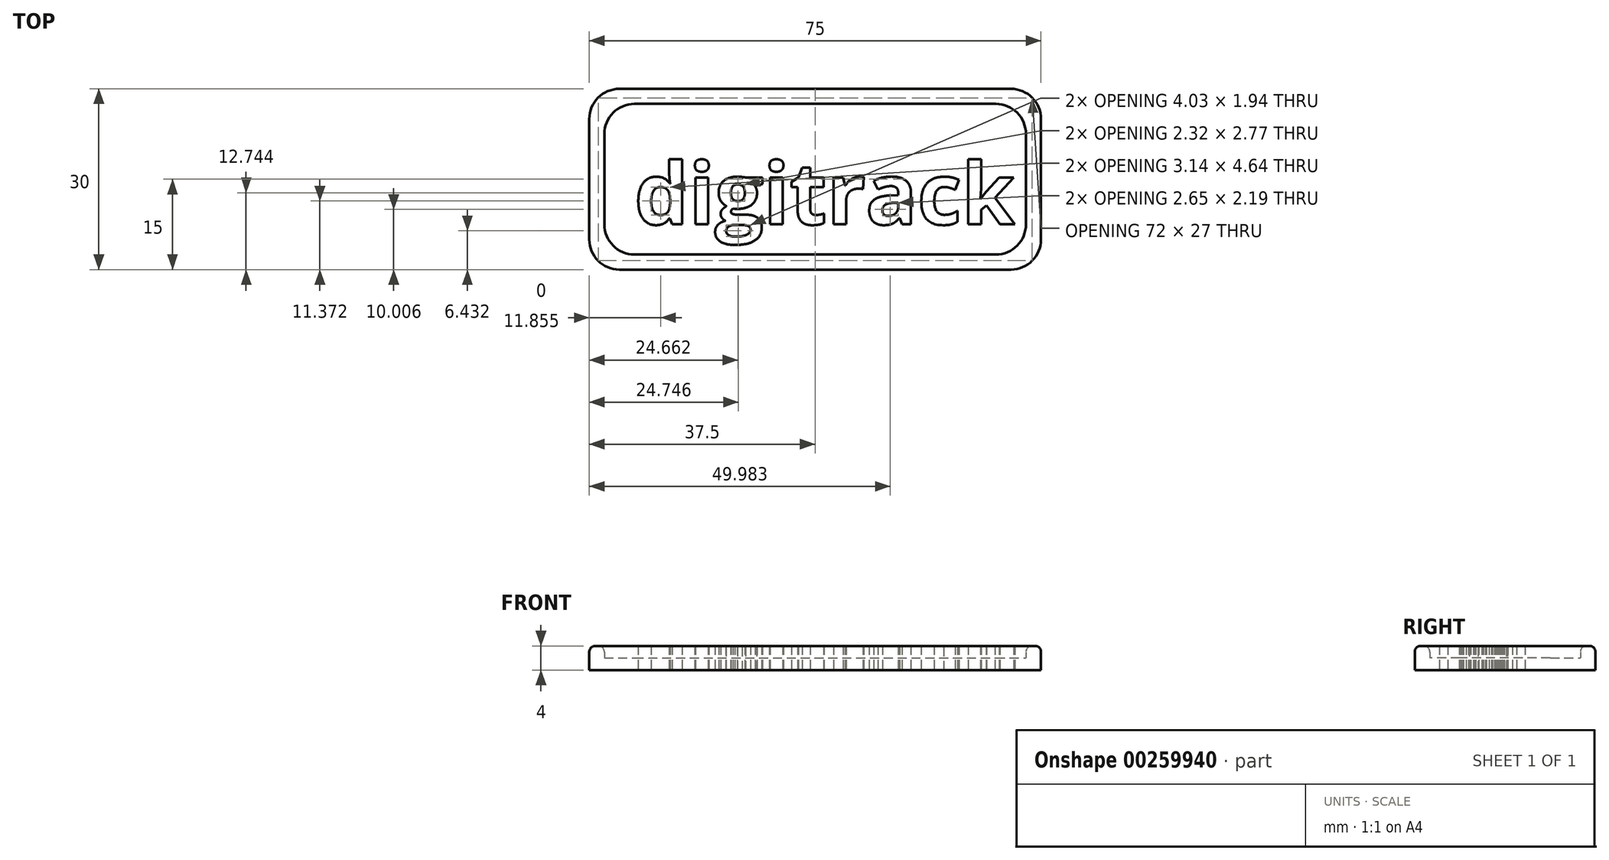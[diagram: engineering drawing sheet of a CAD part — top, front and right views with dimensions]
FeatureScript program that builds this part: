
annotation { "Feature Type Name" : "Feature", "Feature Type Description" : "" }
export const myFeature = defineFeature(function(context is Context, id is Id, definition is map)
    precondition{}
    {
        {
            var Q0;
            Q0=qCreatedBy(makeId("Top.planeOp"),FACE);
            var sketch = newSketch(context, id + "F0", { "sketchPlane" : qUnion([Q0])});
            skText(sketch, "E0", { "text": "digitrack", "fontName": "OpenSans-Bold.ttf"});
            const initialGuessF0  = {"E0": [0, 0, 1, 0, 0.0205]};
            skSetInitialGuess(sketch, initialGuessF0);
            skSolve(sketch);
        }
        {
            var Q0;
            Q0 = qSketchRegion(id + "F0", true);
            extrude(context, id + "F1", {"entities" : qUnion([Q0]), "depth" : 8 * mm});
        }
        {
            var Q0;
            Q0=makeQuery(id+"F1.opExtrude","SWEPT_BODY",BODY,{"disambiguationData":[OSD([sQuery(id+"F0.wireOp",EDGE,"E0.sketch_text.stroke-0"),sQuery(id+"F0.wireOp",EDGE,"E0.sketch_text.stroke-1"),sQuery(id+"F0.wireOp",EDGE,"E0.sketch_text.stroke-2"),sQuery(id+"F0.wireOp",EDGE,"E0.sketch_text.stroke-3"),sQuery(id+"F0.wireOp",EDGE,"E0.sketch_text.stroke-4"),sQuery(id+"F0.wireOp",EDGE,"E0.sketch_text.stroke-5"),sQuery(id+"F0.wireOp",EDGE,"E0.sketch_text.stroke-6"),sQuery(id+"F0.wireOp",EDGE,"E0.sketch_text.stroke-7"),sQuery(id+"F0.wireOp",EDGE,"E0.sketch_text.stroke-8"),sQuery(id+"F0.wireOp",EDGE,"E0.sketch_text.stroke-9"),sQuery(id+"F0.wireOp",EDGE,"E0.sketch_text.stroke-10"),sQuery(id+"F0.wireOp",EDGE,"E0.sketch_text.stroke-11"),sQuery(id+"F0.wireOp",EDGE,"E0.sketch_text.stroke-12"),sQuery(id+"F0.wireOp",EDGE,"E0.sketch_text.stroke-13"),sQuery(id+"F0.wireOp",EDGE,"E0.sketch_text.stroke-14"),sQuery(id+"F0.wireOp",EDGE,"E0.sketch_text.stroke-15"),sQuery(id+"F0.wireOp",EDGE,"E0.sketch_text.stroke-16"),sQuery(id+"F0.wireOp",EDGE,"E0.sketch_text.stroke-17"),sQuery(id+"F0.wireOp",EDGE,"E0.sketch_text.stroke-18"),sQuery(id+"F0.wireOp",EDGE,"E0.sketch_text.stroke-19"),sQuery(id+"F0.wireOp",EDGE,"E0.sketch_text.stroke-20"),sQuery(id+"F0.wireOp",EDGE,"E0.sketch_text.stroke-21"),sQuery(id+"F0.wireOp",EDGE,"E0.sketch_text.stroke-22")])]});
            var Q1;
            Q1=makeQuery(id+"F1.opExtrude","SWEPT_BODY",BODY,{"disambiguationData":[OSD([sQuery(id+"F0.wireOp",EDGE,"E0.sketch_text.stroke-23"),sQuery(id+"F0.wireOp",EDGE,"E0.sketch_text.stroke-24"),sQuery(id+"F0.wireOp",EDGE,"E0.sketch_text.stroke-25"),sQuery(id+"F0.wireOp",EDGE,"E0.sketch_text.stroke-26"),sQuery(id+"F0.wireOp",EDGE,"E0.sketch_text.stroke-27")])]});
            var Q2;
            Q2=makeQuery(id+"F1.opExtrude","SWEPT_BODY",BODY,{"disambiguationData":[OSD([sQuery(id+"F0.wireOp",EDGE,"E0.sketch_text.stroke-28"),sQuery(id+"F0.wireOp",EDGE,"E0.sketch_text.stroke-29"),sQuery(id+"F0.wireOp",EDGE,"E0.sketch_text.stroke-30"),sQuery(id+"F0.wireOp",EDGE,"E0.sketch_text.stroke-31")])]});
            var Q3;
            Q3=makeQuery(id+"F1.opExtrude","SWEPT_BODY",BODY,{"disambiguationData":[OSD([sQuery(id+"F0.wireOp",EDGE,"E0.sketch_text.stroke-32"),sQuery(id+"F0.wireOp",EDGE,"E0.sketch_text.stroke-33"),sQuery(id+"F0.wireOp",EDGE,"E0.sketch_text.stroke-34"),sQuery(id+"F0.wireOp",EDGE,"E0.sketch_text.stroke-35"),sQuery(id+"F0.wireOp",EDGE,"E0.sketch_text.stroke-36"),sQuery(id+"F0.wireOp",EDGE,"E0.sketch_text.stroke-37"),sQuery(id+"F0.wireOp",EDGE,"E0.sketch_text.stroke-38"),sQuery(id+"F0.wireOp",EDGE,"E0.sketch_text.stroke-39"),sQuery(id+"F0.wireOp",EDGE,"E0.sketch_text.stroke-40"),sQuery(id+"F0.wireOp",EDGE,"E0.sketch_text.stroke-41"),sQuery(id+"F0.wireOp",EDGE,"E0.sketch_text.stroke-42"),sQuery(id+"F0.wireOp",EDGE,"E0.sketch_text.stroke-43"),sQuery(id+"F0.wireOp",EDGE,"E0.sketch_text.stroke-44"),sQuery(id+"F0.wireOp",EDGE,"E0.sketch_text.stroke-45"),sQuery(id+"F0.wireOp",EDGE,"E0.sketch_text.stroke-46"),sQuery(id+"F0.wireOp",EDGE,"E0.sketch_text.stroke-47"),sQuery(id+"F0.wireOp",EDGE,"E0.sketch_text.stroke-48"),sQuery(id+"F0.wireOp",EDGE,"E0.sketch_text.stroke-49"),sQuery(id+"F0.wireOp",EDGE,"E0.sketch_text.stroke-50"),sQuery(id+"F0.wireOp",EDGE,"E0.sketch_text.stroke-51"),sQuery(id+"F0.wireOp",EDGE,"E0.sketch_text.stroke-52"),sQuery(id+"F0.wireOp",EDGE,"E0.sketch_text.stroke-53"),sQuery(id+"F0.wireOp",EDGE,"E0.sketch_text.stroke-54"),sQuery(id+"F0.wireOp",EDGE,"E0.sketch_text.stroke-55"),sQuery(id+"F0.wireOp",EDGE,"E0.sketch_text.stroke-56"),sQuery(id+"F0.wireOp",EDGE,"E0.sketch_text.stroke-57"),sQuery(id+"F0.wireOp",EDGE,"E0.sketch_text.stroke-58"),sQuery(id+"F0.wireOp",EDGE,"E0.sketch_text.stroke-59"),sQuery(id+"F0.wireOp",EDGE,"E0.sketch_text.stroke-60"),sQuery(id+"F0.wireOp",EDGE,"E0.sketch_text.stroke-61"),sQuery(id+"F0.wireOp",EDGE,"E0.sketch_text.stroke-62"),sQuery(id+"F0.wireOp",EDGE,"E0.sketch_text.stroke-63"),sQuery(id+"F0.wireOp",EDGE,"E0.sketch_text.stroke-64"),sQuery(id+"F0.wireOp",EDGE,"E0.sketch_text.stroke-65"),sQuery(id+"F0.wireOp",EDGE,"E0.sketch_text.stroke-66"),sQuery(id+"F0.wireOp",EDGE,"E0.sketch_text.stroke-67"),sQuery(id+"F0.wireOp",EDGE,"E0.sketch_text.stroke-68"),sQuery(id+"F0.wireOp",EDGE,"E0.sketch_text.stroke-69"),sQuery(id+"F0.wireOp",EDGE,"E0.sketch_text.stroke-70"),sQuery(id+"F0.wireOp",EDGE,"E0.sketch_text.stroke-71"),sQuery(id+"F0.wireOp",EDGE,"E0.sketch_text.stroke-72"),sQuery(id+"F0.wireOp",EDGE,"E0.sketch_text.stroke-73"),sQuery(id+"F0.wireOp",EDGE,"E0.sketch_text.stroke-74"),sQuery(id+"F0.wireOp",EDGE,"E0.sketch_text.stroke-75")])]});
            var Q4;
            Q4=makeQuery(id+"F1.opExtrude","SWEPT_BODY",BODY,{"disambiguationData":[OSD([sQuery(id+"F0.wireOp",EDGE,"E0.sketch_text.stroke-76"),sQuery(id+"F0.wireOp",EDGE,"E0.sketch_text.stroke-77"),sQuery(id+"F0.wireOp",EDGE,"E0.sketch_text.stroke-78"),sQuery(id+"F0.wireOp",EDGE,"E0.sketch_text.stroke-79"),sQuery(id+"F0.wireOp",EDGE,"E0.sketch_text.stroke-80")])]});
            var Q5;
            Q5=makeQuery(id+"F1.opExtrude","SWEPT_BODY",BODY,{"disambiguationData":[OSD([sQuery(id+"F0.wireOp",EDGE,"E0.sketch_text.stroke-81"),sQuery(id+"F0.wireOp",EDGE,"E0.sketch_text.stroke-82"),sQuery(id+"F0.wireOp",EDGE,"E0.sketch_text.stroke-83"),sQuery(id+"F0.wireOp",EDGE,"E0.sketch_text.stroke-84")])]});
            var Q6;
            Q6=makeQuery(id+"F1.opExtrude","SWEPT_BODY",BODY,{"disambiguationData":[OSD([sQuery(id+"F0.wireOp",EDGE,"E0.sketch_text.stroke-85"),sQuery(id+"F0.wireOp",EDGE,"E0.sketch_text.stroke-86"),sQuery(id+"F0.wireOp",EDGE,"E0.sketch_text.stroke-87"),sQuery(id+"F0.wireOp",EDGE,"E0.sketch_text.stroke-88"),sQuery(id+"F0.wireOp",EDGE,"E0.sketch_text.stroke-89"),sQuery(id+"F0.wireOp",EDGE,"E0.sketch_text.stroke-90"),sQuery(id+"F0.wireOp",EDGE,"E0.sketch_text.stroke-91"),sQuery(id+"F0.wireOp",EDGE,"E0.sketch_text.stroke-92"),sQuery(id+"F0.wireOp",EDGE,"E0.sketch_text.stroke-93"),sQuery(id+"F0.wireOp",EDGE,"E0.sketch_text.stroke-94"),sQuery(id+"F0.wireOp",EDGE,"E0.sketch_text.stroke-95"),sQuery(id+"F0.wireOp",EDGE,"E0.sketch_text.stroke-96"),sQuery(id+"F0.wireOp",EDGE,"E0.sketch_text.stroke-97"),sQuery(id+"F0.wireOp",EDGE,"E0.sketch_text.stroke-98"),sQuery(id+"F0.wireOp",EDGE,"E0.sketch_text.stroke-99"),sQuery(id+"F0.wireOp",EDGE,"E0.sketch_text.stroke-100"),sQuery(id+"F0.wireOp",EDGE,"E0.sketch_text.stroke-101"),sQuery(id+"F0.wireOp",EDGE,"E0.sketch_text.stroke-102")])]});
            var Q7;
            Q7=makeQuery(id+"F1.opExtrude","SWEPT_BODY",BODY,{"disambiguationData":[OSD([sQuery(id+"F0.wireOp",EDGE,"E0.sketch_text.stroke-103"),sQuery(id+"F0.wireOp",EDGE,"E0.sketch_text.stroke-104"),sQuery(id+"F0.wireOp",EDGE,"E0.sketch_text.stroke-105"),sQuery(id+"F0.wireOp",EDGE,"E0.sketch_text.stroke-106"),sQuery(id+"F0.wireOp",EDGE,"E0.sketch_text.stroke-107"),sQuery(id+"F0.wireOp",EDGE,"E0.sketch_text.stroke-108"),sQuery(id+"F0.wireOp",EDGE,"E0.sketch_text.stroke-109"),sQuery(id+"F0.wireOp",EDGE,"E0.sketch_text.stroke-110"),sQuery(id+"F0.wireOp",EDGE,"E0.sketch_text.stroke-111"),sQuery(id+"F0.wireOp",EDGE,"E0.sketch_text.stroke-112"),sQuery(id+"F0.wireOp",EDGE,"E0.sketch_text.stroke-113"),sQuery(id+"F0.wireOp",EDGE,"E0.sketch_text.stroke-114"),sQuery(id+"F0.wireOp",EDGE,"E0.sketch_text.stroke-115")])]});
            var Q8;
            Q8=makeQuery(id+"F1.opExtrude","SWEPT_BODY",BODY,{"disambiguationData":[OSD([sQuery(id+"F0.wireOp",EDGE,"E0.sketch_text.stroke-116"),sQuery(id+"F0.wireOp",EDGE,"E0.sketch_text.stroke-117"),sQuery(id+"F0.wireOp",EDGE,"E0.sketch_text.stroke-118"),sQuery(id+"F0.wireOp",EDGE,"E0.sketch_text.stroke-119"),sQuery(id+"F0.wireOp",EDGE,"E0.sketch_text.stroke-120"),sQuery(id+"F0.wireOp",EDGE,"E0.sketch_text.stroke-121"),sQuery(id+"F0.wireOp",EDGE,"E0.sketch_text.stroke-122"),sQuery(id+"F0.wireOp",EDGE,"E0.sketch_text.stroke-123"),sQuery(id+"F0.wireOp",EDGE,"E0.sketch_text.stroke-124"),sQuery(id+"F0.wireOp",EDGE,"E0.sketch_text.stroke-125"),sQuery(id+"F0.wireOp",EDGE,"E0.sketch_text.stroke-126"),sQuery(id+"F0.wireOp",EDGE,"E0.sketch_text.stroke-127"),sQuery(id+"F0.wireOp",EDGE,"E0.sketch_text.stroke-128"),sQuery(id+"F0.wireOp",EDGE,"E0.sketch_text.stroke-129"),sQuery(id+"F0.wireOp",EDGE,"E0.sketch_text.stroke-130"),sQuery(id+"F0.wireOp",EDGE,"E0.sketch_text.stroke-131"),sQuery(id+"F0.wireOp",EDGE,"E0.sketch_text.stroke-132"),sQuery(id+"F0.wireOp",EDGE,"E0.sketch_text.stroke-133"),sQuery(id+"F0.wireOp",EDGE,"E0.sketch_text.stroke-134"),sQuery(id+"F0.wireOp",EDGE,"E0.sketch_text.stroke-135"),sQuery(id+"F0.wireOp",EDGE,"E0.sketch_text.stroke-136"),sQuery(id+"F0.wireOp",EDGE,"E0.sketch_text.stroke-137"),sQuery(id+"F0.wireOp",EDGE,"E0.sketch_text.stroke-138"),sQuery(id+"F0.wireOp",EDGE,"E0.sketch_text.stroke-139"),sQuery(id+"F0.wireOp",EDGE,"E0.sketch_text.stroke-140")])]});
            var Q9;
            Q9=makeQuery(id+"F1.opExtrude","SWEPT_BODY",BODY,{"disambiguationData":[OSD([sQuery(id+"F0.wireOp",EDGE,"E0.sketch_text.stroke-141"),sQuery(id+"F0.wireOp",EDGE,"E0.sketch_text.stroke-142"),sQuery(id+"F0.wireOp",EDGE,"E0.sketch_text.stroke-143"),sQuery(id+"F0.wireOp",EDGE,"E0.sketch_text.stroke-144"),sQuery(id+"F0.wireOp",EDGE,"E0.sketch_text.stroke-145"),sQuery(id+"F0.wireOp",EDGE,"E0.sketch_text.stroke-146"),sQuery(id+"F0.wireOp",EDGE,"E0.sketch_text.stroke-147"),sQuery(id+"F0.wireOp",EDGE,"E0.sketch_text.stroke-148"),sQuery(id+"F0.wireOp",EDGE,"E0.sketch_text.stroke-149"),sQuery(id+"F0.wireOp",EDGE,"E0.sketch_text.stroke-150"),sQuery(id+"F0.wireOp",EDGE,"E0.sketch_text.stroke-151"),sQuery(id+"F0.wireOp",EDGE,"E0.sketch_text.stroke-152"),sQuery(id+"F0.wireOp",EDGE,"E0.sketch_text.stroke-153"),sQuery(id+"F0.wireOp",EDGE,"E0.sketch_text.stroke-154")])]});
            var Q10;
            Q10=makeQuery(id+"F1.opExtrude","SWEPT_BODY",BODY,{"disambiguationData":[OSD([sQuery(id+"F0.wireOp",EDGE,"E0.sketch_text.stroke-155"),sQuery(id+"F0.wireOp",EDGE,"E0.sketch_text.stroke-156"),sQuery(id+"F0.wireOp",EDGE,"E0.sketch_text.stroke-157"),sQuery(id+"F0.wireOp",EDGE,"E0.sketch_text.stroke-158"),sQuery(id+"F0.wireOp",EDGE,"E0.sketch_text.stroke-159"),sQuery(id+"F0.wireOp",EDGE,"E0.sketch_text.stroke-160"),sQuery(id+"F0.wireOp",EDGE,"E0.sketch_text.stroke-161"),sQuery(id+"F0.wireOp",EDGE,"E0.sketch_text.stroke-162"),sQuery(id+"F0.wireOp",EDGE,"E0.sketch_text.stroke-163"),sQuery(id+"F0.wireOp",EDGE,"E0.sketch_text.stroke-164"),sQuery(id+"F0.wireOp",EDGE,"E0.sketch_text.stroke-165"),sQuery(id+"F0.wireOp",EDGE,"E0.sketch_text.stroke-166"),sQuery(id+"F0.wireOp",EDGE,"E0.sketch_text.stroke-167"),sQuery(id+"F0.wireOp",EDGE,"E0.sketch_text.stroke-168"),sQuery(id+"F0.wireOp",EDGE,"E0.sketch_text.stroke-169")])]});
            var Q11;
            Q11=qCreatedBy(makeId("Origin.pointOp"),VERTEX);
            transform(context, id + "F2", {"entities" : qUnion([Q0, Q1, Q2, Q3, Q4, Q5, Q6, Q7, Q8, Q9, Q10]), "transformType" : TransformType.SCALE_UNIFORMLY, "scale" : 0.5, "scalePoint" : qUnion([Q11]), "makeCopy" : false});
        }
        {
            var Q0;
            Q0=makeQuery(id+"F1.opExtrude","SWEPT_BODY",BODY,{"disambiguationData":[OSD([sQuery(id+"F0.wireOp",EDGE,"E0.sketch_text.stroke-155"),sQuery(id+"F0.wireOp",EDGE,"E0.sketch_text.stroke-156"),sQuery(id+"F0.wireOp",EDGE,"E0.sketch_text.stroke-157"),sQuery(id+"F0.wireOp",EDGE,"E0.sketch_text.stroke-158"),sQuery(id+"F0.wireOp",EDGE,"E0.sketch_text.stroke-159"),sQuery(id+"F0.wireOp",EDGE,"E0.sketch_text.stroke-160"),sQuery(id+"F0.wireOp",EDGE,"E0.sketch_text.stroke-161"),sQuery(id+"F0.wireOp",EDGE,"E0.sketch_text.stroke-162"),sQuery(id+"F0.wireOp",EDGE,"E0.sketch_text.stroke-163"),sQuery(id+"F0.wireOp",EDGE,"E0.sketch_text.stroke-164"),sQuery(id+"F0.wireOp",EDGE,"E0.sketch_text.stroke-165"),sQuery(id+"F0.wireOp",EDGE,"E0.sketch_text.stroke-166"),sQuery(id+"F0.wireOp",EDGE,"E0.sketch_text.stroke-167"),sQuery(id+"F0.wireOp",EDGE,"E0.sketch_text.stroke-168"),sQuery(id+"F0.wireOp",EDGE,"E0.sketch_text.stroke-169")])]});
            var Q1;
            Q1=makeQuery(id+"F1.opExtrude","SWEPT_BODY",BODY,{"disambiguationData":[OSD([sQuery(id+"F0.wireOp",EDGE,"E0.sketch_text.stroke-141"),sQuery(id+"F0.wireOp",EDGE,"E0.sketch_text.stroke-142"),sQuery(id+"F0.wireOp",EDGE,"E0.sketch_text.stroke-143"),sQuery(id+"F0.wireOp",EDGE,"E0.sketch_text.stroke-144"),sQuery(id+"F0.wireOp",EDGE,"E0.sketch_text.stroke-145"),sQuery(id+"F0.wireOp",EDGE,"E0.sketch_text.stroke-146"),sQuery(id+"F0.wireOp",EDGE,"E0.sketch_text.stroke-147"),sQuery(id+"F0.wireOp",EDGE,"E0.sketch_text.stroke-148"),sQuery(id+"F0.wireOp",EDGE,"E0.sketch_text.stroke-149"),sQuery(id+"F0.wireOp",EDGE,"E0.sketch_text.stroke-150"),sQuery(id+"F0.wireOp",EDGE,"E0.sketch_text.stroke-151"),sQuery(id+"F0.wireOp",EDGE,"E0.sketch_text.stroke-152"),sQuery(id+"F0.wireOp",EDGE,"E0.sketch_text.stroke-153"),sQuery(id+"F0.wireOp",EDGE,"E0.sketch_text.stroke-154")])]});
            var Q2;
            Q2=makeQuery(id+"F1.opExtrude","SWEPT_BODY",BODY,{"disambiguationData":[OSD([sQuery(id+"F0.wireOp",EDGE,"E0.sketch_text.stroke-116"),sQuery(id+"F0.wireOp",EDGE,"E0.sketch_text.stroke-117"),sQuery(id+"F0.wireOp",EDGE,"E0.sketch_text.stroke-118"),sQuery(id+"F0.wireOp",EDGE,"E0.sketch_text.stroke-119"),sQuery(id+"F0.wireOp",EDGE,"E0.sketch_text.stroke-120"),sQuery(id+"F0.wireOp",EDGE,"E0.sketch_text.stroke-121"),sQuery(id+"F0.wireOp",EDGE,"E0.sketch_text.stroke-122"),sQuery(id+"F0.wireOp",EDGE,"E0.sketch_text.stroke-123"),sQuery(id+"F0.wireOp",EDGE,"E0.sketch_text.stroke-124"),sQuery(id+"F0.wireOp",EDGE,"E0.sketch_text.stroke-125"),sQuery(id+"F0.wireOp",EDGE,"E0.sketch_text.stroke-126"),sQuery(id+"F0.wireOp",EDGE,"E0.sketch_text.stroke-127"),sQuery(id+"F0.wireOp",EDGE,"E0.sketch_text.stroke-128"),sQuery(id+"F0.wireOp",EDGE,"E0.sketch_text.stroke-129"),sQuery(id+"F0.wireOp",EDGE,"E0.sketch_text.stroke-130"),sQuery(id+"F0.wireOp",EDGE,"E0.sketch_text.stroke-131"),sQuery(id+"F0.wireOp",EDGE,"E0.sketch_text.stroke-132"),sQuery(id+"F0.wireOp",EDGE,"E0.sketch_text.stroke-133"),sQuery(id+"F0.wireOp",EDGE,"E0.sketch_text.stroke-134"),sQuery(id+"F0.wireOp",EDGE,"E0.sketch_text.stroke-135"),sQuery(id+"F0.wireOp",EDGE,"E0.sketch_text.stroke-136"),sQuery(id+"F0.wireOp",EDGE,"E0.sketch_text.stroke-137"),sQuery(id+"F0.wireOp",EDGE,"E0.sketch_text.stroke-138"),sQuery(id+"F0.wireOp",EDGE,"E0.sketch_text.stroke-139"),sQuery(id+"F0.wireOp",EDGE,"E0.sketch_text.stroke-140")])]});
            var Q3;
            Q3=makeQuery(id+"F1.opExtrude","SWEPT_BODY",BODY,{"disambiguationData":[OSD([sQuery(id+"F0.wireOp",EDGE,"E0.sketch_text.stroke-103"),sQuery(id+"F0.wireOp",EDGE,"E0.sketch_text.stroke-104"),sQuery(id+"F0.wireOp",EDGE,"E0.sketch_text.stroke-105"),sQuery(id+"F0.wireOp",EDGE,"E0.sketch_text.stroke-106"),sQuery(id+"F0.wireOp",EDGE,"E0.sketch_text.stroke-107"),sQuery(id+"F0.wireOp",EDGE,"E0.sketch_text.stroke-108"),sQuery(id+"F0.wireOp",EDGE,"E0.sketch_text.stroke-109"),sQuery(id+"F0.wireOp",EDGE,"E0.sketch_text.stroke-110"),sQuery(id+"F0.wireOp",EDGE,"E0.sketch_text.stroke-111"),sQuery(id+"F0.wireOp",EDGE,"E0.sketch_text.stroke-112"),sQuery(id+"F0.wireOp",EDGE,"E0.sketch_text.stroke-113"),sQuery(id+"F0.wireOp",EDGE,"E0.sketch_text.stroke-114"),sQuery(id+"F0.wireOp",EDGE,"E0.sketch_text.stroke-115")])]});
            var Q4;
            Q4=makeQuery(id+"F1.opExtrude","SWEPT_BODY",BODY,{"disambiguationData":[OSD([sQuery(id+"F0.wireOp",EDGE,"E0.sketch_text.stroke-85"),sQuery(id+"F0.wireOp",EDGE,"E0.sketch_text.stroke-86"),sQuery(id+"F0.wireOp",EDGE,"E0.sketch_text.stroke-87"),sQuery(id+"F0.wireOp",EDGE,"E0.sketch_text.stroke-88"),sQuery(id+"F0.wireOp",EDGE,"E0.sketch_text.stroke-89"),sQuery(id+"F0.wireOp",EDGE,"E0.sketch_text.stroke-90"),sQuery(id+"F0.wireOp",EDGE,"E0.sketch_text.stroke-91"),sQuery(id+"F0.wireOp",EDGE,"E0.sketch_text.stroke-92"),sQuery(id+"F0.wireOp",EDGE,"E0.sketch_text.stroke-93"),sQuery(id+"F0.wireOp",EDGE,"E0.sketch_text.stroke-94"),sQuery(id+"F0.wireOp",EDGE,"E0.sketch_text.stroke-95"),sQuery(id+"F0.wireOp",EDGE,"E0.sketch_text.stroke-96"),sQuery(id+"F0.wireOp",EDGE,"E0.sketch_text.stroke-97"),sQuery(id+"F0.wireOp",EDGE,"E0.sketch_text.stroke-98"),sQuery(id+"F0.wireOp",EDGE,"E0.sketch_text.stroke-99"),sQuery(id+"F0.wireOp",EDGE,"E0.sketch_text.stroke-100"),sQuery(id+"F0.wireOp",EDGE,"E0.sketch_text.stroke-101"),sQuery(id+"F0.wireOp",EDGE,"E0.sketch_text.stroke-102")])]});
            var Q5;
            Q5=makeQuery(id+"F1.opExtrude","SWEPT_BODY",BODY,{"disambiguationData":[OSD([sQuery(id+"F0.wireOp",EDGE,"E0.sketch_text.stroke-81"),sQuery(id+"F0.wireOp",EDGE,"E0.sketch_text.stroke-82"),sQuery(id+"F0.wireOp",EDGE,"E0.sketch_text.stroke-83"),sQuery(id+"F0.wireOp",EDGE,"E0.sketch_text.stroke-84")])]});
            var Q6;
            Q6=makeQuery(id+"F1.opExtrude","SWEPT_BODY",BODY,{"disambiguationData":[OSD([sQuery(id+"F0.wireOp",EDGE,"E0.sketch_text.stroke-76"),sQuery(id+"F0.wireOp",EDGE,"E0.sketch_text.stroke-77"),sQuery(id+"F0.wireOp",EDGE,"E0.sketch_text.stroke-78"),sQuery(id+"F0.wireOp",EDGE,"E0.sketch_text.stroke-79"),sQuery(id+"F0.wireOp",EDGE,"E0.sketch_text.stroke-80")])]});
            var Q7;
            Q7=makeQuery(id+"F1.opExtrude","SWEPT_BODY",BODY,{"disambiguationData":[OSD([sQuery(id+"F0.wireOp",EDGE,"E0.sketch_text.stroke-32"),sQuery(id+"F0.wireOp",EDGE,"E0.sketch_text.stroke-33"),sQuery(id+"F0.wireOp",EDGE,"E0.sketch_text.stroke-34"),sQuery(id+"F0.wireOp",EDGE,"E0.sketch_text.stroke-35"),sQuery(id+"F0.wireOp",EDGE,"E0.sketch_text.stroke-36"),sQuery(id+"F0.wireOp",EDGE,"E0.sketch_text.stroke-37"),sQuery(id+"F0.wireOp",EDGE,"E0.sketch_text.stroke-38"),sQuery(id+"F0.wireOp",EDGE,"E0.sketch_text.stroke-39"),sQuery(id+"F0.wireOp",EDGE,"E0.sketch_text.stroke-40"),sQuery(id+"F0.wireOp",EDGE,"E0.sketch_text.stroke-41"),sQuery(id+"F0.wireOp",EDGE,"E0.sketch_text.stroke-42"),sQuery(id+"F0.wireOp",EDGE,"E0.sketch_text.stroke-43"),sQuery(id+"F0.wireOp",EDGE,"E0.sketch_text.stroke-44"),sQuery(id+"F0.wireOp",EDGE,"E0.sketch_text.stroke-45"),sQuery(id+"F0.wireOp",EDGE,"E0.sketch_text.stroke-46"),sQuery(id+"F0.wireOp",EDGE,"E0.sketch_text.stroke-47"),sQuery(id+"F0.wireOp",EDGE,"E0.sketch_text.stroke-48"),sQuery(id+"F0.wireOp",EDGE,"E0.sketch_text.stroke-49"),sQuery(id+"F0.wireOp",EDGE,"E0.sketch_text.stroke-50"),sQuery(id+"F0.wireOp",EDGE,"E0.sketch_text.stroke-51"),sQuery(id+"F0.wireOp",EDGE,"E0.sketch_text.stroke-52"),sQuery(id+"F0.wireOp",EDGE,"E0.sketch_text.stroke-53"),sQuery(id+"F0.wireOp",EDGE,"E0.sketch_text.stroke-54"),sQuery(id+"F0.wireOp",EDGE,"E0.sketch_text.stroke-55"),sQuery(id+"F0.wireOp",EDGE,"E0.sketch_text.stroke-56"),sQuery(id+"F0.wireOp",EDGE,"E0.sketch_text.stroke-57"),sQuery(id+"F0.wireOp",EDGE,"E0.sketch_text.stroke-58"),sQuery(id+"F0.wireOp",EDGE,"E0.sketch_text.stroke-59"),sQuery(id+"F0.wireOp",EDGE,"E0.sketch_text.stroke-60"),sQuery(id+"F0.wireOp",EDGE,"E0.sketch_text.stroke-61"),sQuery(id+"F0.wireOp",EDGE,"E0.sketch_text.stroke-62"),sQuery(id+"F0.wireOp",EDGE,"E0.sketch_text.stroke-63"),sQuery(id+"F0.wireOp",EDGE,"E0.sketch_text.stroke-64"),sQuery(id+"F0.wireOp",EDGE,"E0.sketch_text.stroke-65"),sQuery(id+"F0.wireOp",EDGE,"E0.sketch_text.stroke-66"),sQuery(id+"F0.wireOp",EDGE,"E0.sketch_text.stroke-67"),sQuery(id+"F0.wireOp",EDGE,"E0.sketch_text.stroke-68"),sQuery(id+"F0.wireOp",EDGE,"E0.sketch_text.stroke-69"),sQuery(id+"F0.wireOp",EDGE,"E0.sketch_text.stroke-70"),sQuery(id+"F0.wireOp",EDGE,"E0.sketch_text.stroke-71"),sQuery(id+"F0.wireOp",EDGE,"E0.sketch_text.stroke-72"),sQuery(id+"F0.wireOp",EDGE,"E0.sketch_text.stroke-73"),sQuery(id+"F0.wireOp",EDGE,"E0.sketch_text.stroke-74"),sQuery(id+"F0.wireOp",EDGE,"E0.sketch_text.stroke-75")])]});
            var Q8;
            Q8=makeQuery(id+"F1.opExtrude","SWEPT_BODY",BODY,{"disambiguationData":[OSD([sQuery(id+"F0.wireOp",EDGE,"E0.sketch_text.stroke-28"),sQuery(id+"F0.wireOp",EDGE,"E0.sketch_text.stroke-29"),sQuery(id+"F0.wireOp",EDGE,"E0.sketch_text.stroke-30"),sQuery(id+"F0.wireOp",EDGE,"E0.sketch_text.stroke-31")])]});
            var Q9;
            Q9=makeQuery(id+"F1.opExtrude","SWEPT_BODY",BODY,{"disambiguationData":[OSD([sQuery(id+"F0.wireOp",EDGE,"E0.sketch_text.stroke-23"),sQuery(id+"F0.wireOp",EDGE,"E0.sketch_text.stroke-24"),sQuery(id+"F0.wireOp",EDGE,"E0.sketch_text.stroke-25"),sQuery(id+"F0.wireOp",EDGE,"E0.sketch_text.stroke-26"),sQuery(id+"F0.wireOp",EDGE,"E0.sketch_text.stroke-27")])]});
            var Q10;
            Q10=makeQuery(id+"F1.opExtrude","SWEPT_BODY",BODY,{"disambiguationData":[OSD([sQuery(id+"F0.wireOp",EDGE,"E0.sketch_text.stroke-0"),sQuery(id+"F0.wireOp",EDGE,"E0.sketch_text.stroke-1"),sQuery(id+"F0.wireOp",EDGE,"E0.sketch_text.stroke-2"),sQuery(id+"F0.wireOp",EDGE,"E0.sketch_text.stroke-3"),sQuery(id+"F0.wireOp",EDGE,"E0.sketch_text.stroke-4"),sQuery(id+"F0.wireOp",EDGE,"E0.sketch_text.stroke-5"),sQuery(id+"F0.wireOp",EDGE,"E0.sketch_text.stroke-6"),sQuery(id+"F0.wireOp",EDGE,"E0.sketch_text.stroke-7"),sQuery(id+"F0.wireOp",EDGE,"E0.sketch_text.stroke-8"),sQuery(id+"F0.wireOp",EDGE,"E0.sketch_text.stroke-9"),sQuery(id+"F0.wireOp",EDGE,"E0.sketch_text.stroke-10"),sQuery(id+"F0.wireOp",EDGE,"E0.sketch_text.stroke-11"),sQuery(id+"F0.wireOp",EDGE,"E0.sketch_text.stroke-12"),sQuery(id+"F0.wireOp",EDGE,"E0.sketch_text.stroke-13"),sQuery(id+"F0.wireOp",EDGE,"E0.sketch_text.stroke-14"),sQuery(id+"F0.wireOp",EDGE,"E0.sketch_text.stroke-15"),sQuery(id+"F0.wireOp",EDGE,"E0.sketch_text.stroke-16"),sQuery(id+"F0.wireOp",EDGE,"E0.sketch_text.stroke-17"),sQuery(id+"F0.wireOp",EDGE,"E0.sketch_text.stroke-18"),sQuery(id+"F0.wireOp",EDGE,"E0.sketch_text.stroke-19"),sQuery(id+"F0.wireOp",EDGE,"E0.sketch_text.stroke-20"),sQuery(id+"F0.wireOp",EDGE,"E0.sketch_text.stroke-21"),sQuery(id+"F0.wireOp",EDGE,"E0.sketch_text.stroke-22")])]});
            transform(context, id + "F3", {"entities" : qUnion([Q0, Q1, Q2, Q3, Q4, Q5, Q6, Q7, Q8, Q9, Q10]), "transformType" : TransformType.TRANSLATION_3D, "dx" : -30 * mm, "dy" : -7.5 * mm, "dz" : 0 * mm, "makeCopy" : false});
        }
        {
            var Q0;
            Q0=qCreatedBy(makeId("Top.planeOp"),FACE);
            var sketch = newSketch(context, id + "F4", { "sketchPlane" : qUnion([Q0])});
            skLineSegment(sketch, "E1.bottom", {"start": v(37.5, -15) * mm, "end": v(-37.5, -15) * mm});
            skLineSegment(sketch, "E1.top", {"start": v(37.5, 15) * mm, "end": v(-37.5, 15) * mm});
            skLineSegment(sketch, "E1.left", {"start": v(37.5, -15) * mm, "end": v(37.5, 15) * mm});
            skLineSegment(sketch, "E1.right", {"start": v(-37.5, -15) * mm, "end": v(-37.5, 15) * mm});
            skPoint(sketch, "E1.middle", {"position": v(0, 0) * mm});
            skSolve(sketch);
        }
        {
            var Q0;
            Q0 = qSketchRegion(id + "F4", true);
            extrude(context, id + "F5", {"entities" : qUnion([Q0]), "depth" : 2 * mm});
        }
        {
            var Q0;
            Q0=qCreatedBy(makeId("Top.planeOp"),FACE);
            var sketch = newSketch(context, id + "F6", { "sketchPlane" : qUnion([Q0])});
            skLineSegment(sketch, "E2.bottom", {"start": v(37.5, -15) * mm, "end": v(-37.5, -15) * mm});
            skLineSegment(sketch, "E2.top", {"start": v(37.5, 15) * mm, "end": v(-37.5, 15) * mm});
            skLineSegment(sketch, "E2.left", {"start": v(37.5, -15) * mm, "end": v(37.5, 15) * mm});
            skLineSegment(sketch, "E2.right", {"start": v(-37.5, -15) * mm, "end": v(-37.5, 15) * mm});
            skPoint(sketch, "E2.middle", {"position": v(0, 0) * mm});
            skLineSegment(sketch, "E3.bottom", {"start": v(35, -12.5) * mm, "end": v(-35, -12.5) * mm});
            skLineSegment(sketch, "E3.top", {"start": v(35, 12.5) * mm, "end": v(-35, 12.5) * mm});
            skLineSegment(sketch, "E3.left", {"start": v(35, -12.5) * mm, "end": v(35, 12.5) * mm});
            skLineSegment(sketch, "E3.right", {"start": v(-35, -12.5) * mm, "end": v(-35, 12.5) * mm});
            skSolve(sketch);
        }
        {
            var Q0;
            Q0 = qSketchRegion(id + "F6", true);
            extrude(context, id + "F7", {"entities" : qUnion([Q0]), "depth" : 4 * mm});
        }
        {
            var Q0;
            Q0=makeQuery(id+"F5.opExtrude","SWEPT_BODY",BODY,{"disambiguationData":[OSD([sQuery(id+"F4.wireOp",EDGE,"E1.bottom"),sQuery(id+"F4.wireOp",EDGE,"E1.top"),sQuery(id+"F4.wireOp",EDGE,"E1.left"),sQuery(id+"F4.wireOp",EDGE,"E1.right")])]});
            var Q1;
            Q1=makeQuery(id+"F7.opExtrude","SWEPT_BODY",BODY,{"disambiguationData":[OSD([sQuery(id+"F6.wireOp",EDGE,"E2.bottom"),sQuery(id+"F6.wireOp",EDGE,"E2.top"),sQuery(id+"F6.wireOp",EDGE,"E2.left"),sQuery(id+"F6.wireOp",EDGE,"E2.right"),sQuery(id+"F6.wireOp",EDGE,"E3.bottom"),sQuery(id+"F6.wireOp",EDGE,"E3.top"),sQuery(id+"F6.wireOp",EDGE,"E3.left"),sQuery(id+"F6.wireOp",EDGE,"E3.right")])]});
            booleanBodies(context, id + "F8", {"operationType" : BooleanOperationType.UNION, "tools" : qUnion([Q0, Q1])});
        }
        {
            var Q0;
            Q0=makeQuery(id+"F8.opBoolean","MERGE",EDGE,{"derivedFrom":[makeQuery(id+"F5.opExtrude","SWEPT_EDGE",EDGE,{"disambiguationData":[OSD([sQuery(id+"F4.wireOp",EDGE,"E1.bottom"),sQuery(id+"F4.wireOp",EDGE,"E1.left")])]}),makeQuery(id+"F7.opExtrude","SWEPT_EDGE",EDGE,{"disambiguationData":[OSD([sQuery(id+"F6.wireOp",EDGE,"E2.bottom"),sQuery(id+"F6.wireOp",EDGE,"E2.left")])]})]});
            var Q1;
            Q1=makeQuery(id+"F7.opExtrude","SWEPT_EDGE",EDGE,{"disambiguationData":[OSD([sQuery(id+"F6.wireOp",EDGE,"E3.top"),sQuery(id+"F6.wireOp",EDGE,"E3.right")])]});
            var Q2;
            Q2=makeQuery(id+"F7.opExtrude","SWEPT_EDGE",EDGE,{"disambiguationData":[OSD([sQuery(id+"F6.wireOp",EDGE,"E3.top"),sQuery(id+"F6.wireOp",EDGE,"E3.left")])]});
            var Q3;
            Q3=makeQuery(id+"F7.opExtrude","SWEPT_EDGE",EDGE,{"disambiguationData":[OSD([sQuery(id+"F6.wireOp",EDGE,"E3.bottom"),sQuery(id+"F6.wireOp",EDGE,"E3.left")])]});
            var Q4;
            Q4=makeQuery(id+"F7.opExtrude","SWEPT_EDGE",EDGE,{"disambiguationData":[OSD([sQuery(id+"F6.wireOp",EDGE,"E3.bottom"),sQuery(id+"F6.wireOp",EDGE,"E3.right")])]});
            var Q5;
            Q5=makeQuery(id+"F8.opBoolean","MERGE",EDGE,{"derivedFrom":[makeQuery(id+"F5.opExtrude","SWEPT_EDGE",EDGE,{"disambiguationData":[OSD([sQuery(id+"F4.wireOp",EDGE,"E1.bottom"),sQuery(id+"F4.wireOp",EDGE,"E1.right")])]}),makeQuery(id+"F7.opExtrude","SWEPT_EDGE",EDGE,{"disambiguationData":[OSD([sQuery(id+"F6.wireOp",EDGE,"E2.bottom"),sQuery(id+"F6.wireOp",EDGE,"E2.right")])]})]});
            var Q6;
            Q6=makeQuery(id+"F8.opBoolean","MERGE",EDGE,{"derivedFrom":[makeQuery(id+"F5.opExtrude","SWEPT_EDGE",EDGE,{"disambiguationData":[OSD([sQuery(id+"F4.wireOp",EDGE,"E1.top"),sQuery(id+"F4.wireOp",EDGE,"E1.right")])]}),makeQuery(id+"F7.opExtrude","SWEPT_EDGE",EDGE,{"disambiguationData":[OSD([sQuery(id+"F6.wireOp",EDGE,"E2.top"),sQuery(id+"F6.wireOp",EDGE,"E2.right")])]})]});
            var Q7;
            Q7=makeQuery(id+"F8.opBoolean","MERGE",EDGE,{"derivedFrom":[makeQuery(id+"F5.opExtrude","SWEPT_EDGE",EDGE,{"disambiguationData":[OSD([sQuery(id+"F4.wireOp",EDGE,"E1.top"),sQuery(id+"F4.wireOp",EDGE,"E1.left")])]}),makeQuery(id+"F7.opExtrude","SWEPT_EDGE",EDGE,{"disambiguationData":[OSD([sQuery(id+"F6.wireOp",EDGE,"E2.top"),sQuery(id+"F6.wireOp",EDGE,"E2.left")])]})]});
            fillet(context, id + "F9", {"entities" : qUnion([Q0, Q1, Q2, Q3, Q4, Q5, Q6, Q7]), "radius" : 5 * mm, "tangentPropagation" : true, "allowEdgeOverflow" : false});
        }
        {
            var Q0;
            Q0=makeQuery(id+"F7.opExtrude","CAP_EDGE",EDGE,{"disambiguationData":[OSD([sQuery(id+"F6.wireOp",EDGE,"E2.bottom")])],"isStart":false});
            var Q1;
            Q1=makeQuery(id+"F7.opExtrude","CAP_EDGE",EDGE,{"disambiguationData":[OSD([sQuery(id+"F6.wireOp",EDGE,"E3.top")])],"isStart":false});
            fillet(context, id + "F10", {"entities" : qUnion([Q0, Q1]), "radius" : 1 * mm, "tangentPropagation" : true, "allowEdgeOverflow" : false});
        }
    });
